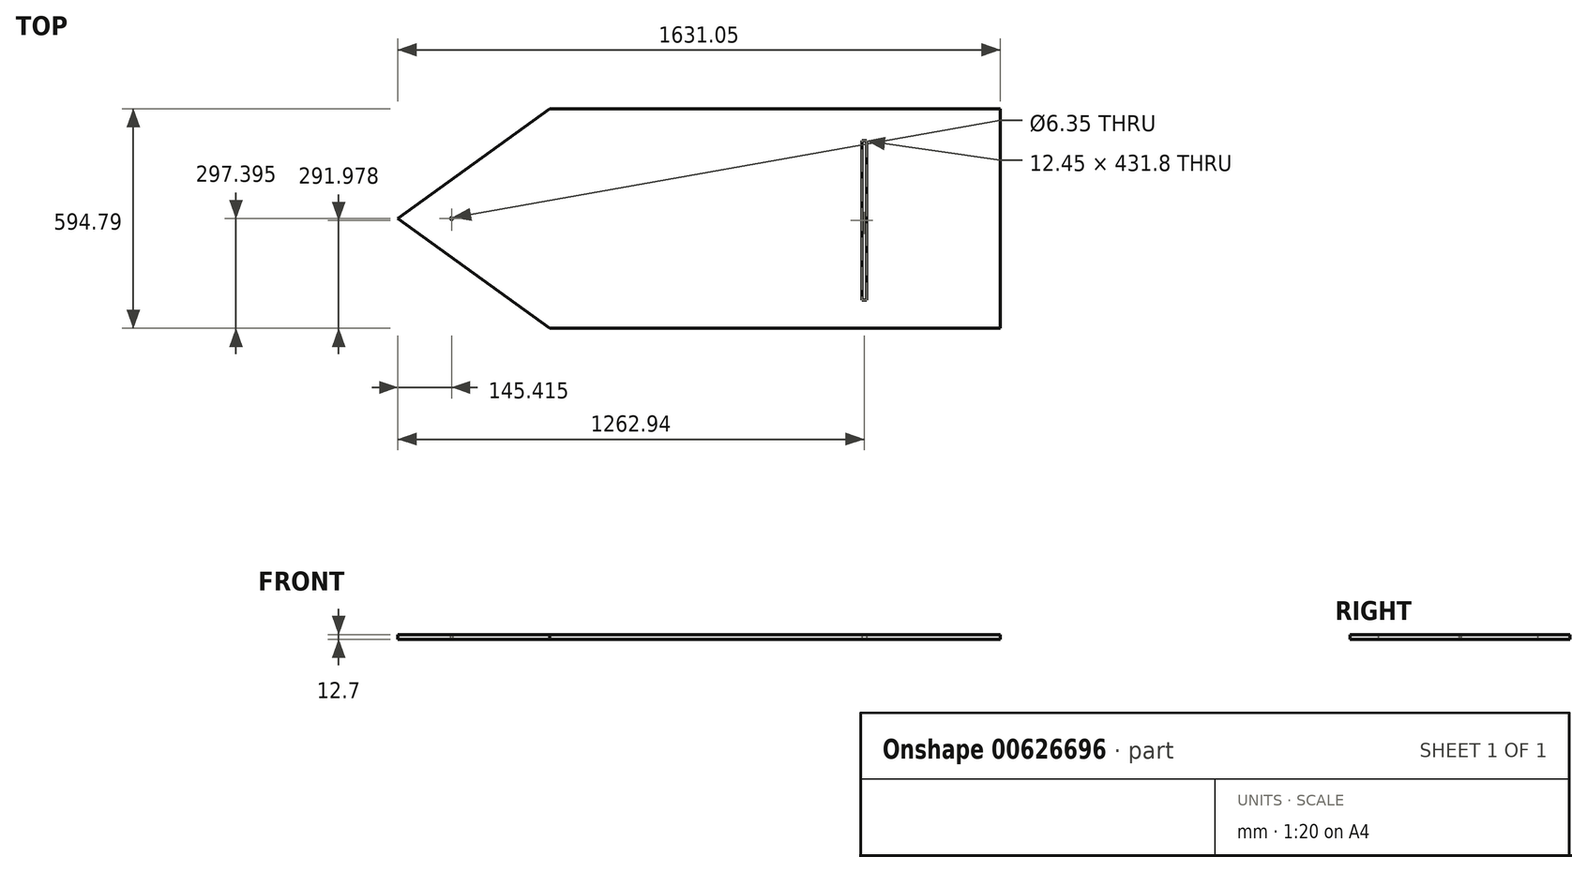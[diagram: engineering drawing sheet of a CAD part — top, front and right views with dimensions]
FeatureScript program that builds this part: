
annotation { "Feature Type Name" : "Feature", "Feature Type Description" : "" }
export const myFeature = defineFeature(function(context is Context, id is Id, definition is map)
    precondition{}
    {
        {
            var Q0;
            Q0=qCreatedBy(makeId("Top.planeOp"),FACE);
            var sketch = newSketch(context, id + "F0", { "sketchPlane" : qUnion([Q0])});
            skLineSegment(sketch, "E0.bottom", {"start": v(-616.22, 190.38) * mm, "end": v(602.98, 190.38) * mm});
            skLineSegment(sketch, "E0.top", {"start": v(-616.22, -404.41) * mm, "end": v(602.98, -404.41) * mm});
            skLineSegment(sketch, "E0.right", {"start": v(602.98, 190.38) * mm, "end": v(602.98, -404.41) * mm});
            skLineSegment(sketch, "E1", {"start": v(-616.22, 190.38) * mm, "end": v(-1028.07, -107.02) * mm});
            skPoint(sketch, "E1.endSnap0", {"position": v(-605.97, -107.02) * mm});
            skLineSegment(sketch, "E2", {"start": v(-1028.07, -107.02) * mm, "end": v(-616.22, -404.41) * mm});
            skLineSegment(sketch, "E3.bottom", {"start": v(228.64, -328.33) * mm, "end": v(241.1, -328.33) * mm});
            skLineSegment(sketch, "E3.top", {"start": v(228.64, 103.47) * mm, "end": v(241.1, 103.47) * mm});
            skLineSegment(sketch, "E3.left", {"start": v(228.64, -328.33) * mm, "end": v(228.64, 103.47) * mm});
            skLineSegment(sketch, "E3.right", {"start": v(241.1, -328.33) * mm, "end": v(241.1, 103.47) * mm});
            skCircle(sketch, "E4", {"center": v(-882.66, -107.02) * mm, "radius": 3.18 * mm});
            skSolve(sketch);
        }
        {
            var Q0;
            Q0=qSketchRegion(id+"F0",true);
            extrude(context, id + "F1", {"entities" : qUnion([Q0]), "depth" : 12.7 * mm, "offsetDistance" : 25.4 * mm});
        }
    });
